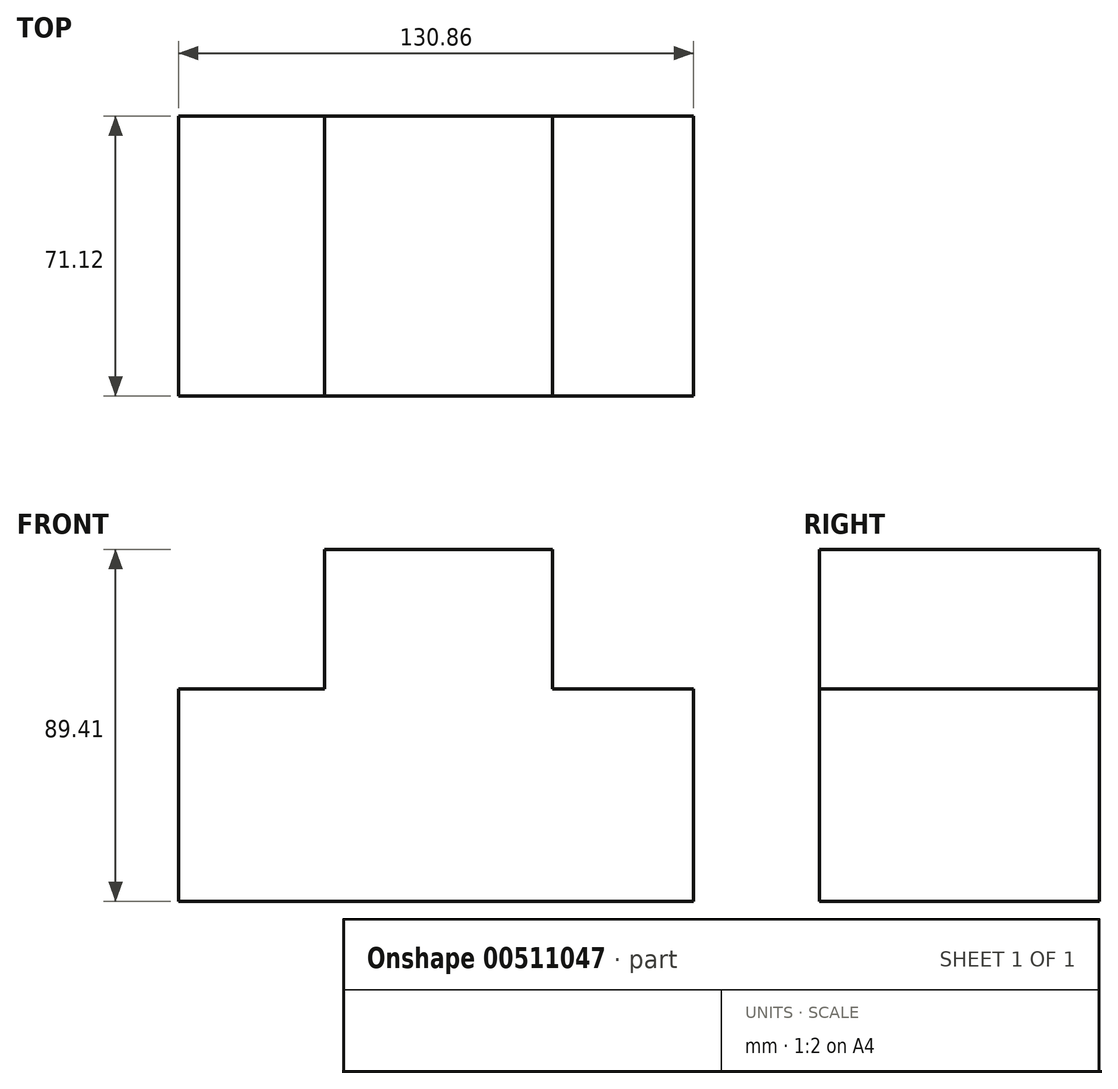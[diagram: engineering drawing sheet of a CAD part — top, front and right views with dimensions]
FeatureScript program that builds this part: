
annotation { "Feature Type Name" : "Feature", "Feature Type Description" : "" }
export const myFeature = defineFeature(function(context is Context, id is Id, definition is map)
    precondition{}
    {
        {
            var Q0;
            Q0=qCreatedBy(makeId("Front.planeOp"),FACE);
            var sketch = newSketch(context, id + "F0", { "sketchPlane" : qUnion([Q0])});
            skLineSegment(sketch, "E0.bottom", {"start": v(-66.27, 59.04) * mm, "end": v(64.59, 59.04) * mm});
            skLineSegment(sketch, "E0.top", {"start": v(-66.27, -48.92) * mm, "end": v(64.59, -48.92) * mm});
            skLineSegment(sketch, "E0.left", {"start": v(-66.27, 59.04) * mm, "end": v(-66.27, -48.92) * mm});
            skLineSegment(sketch, "E0.right", {"start": v(64.59, 59.04) * mm, "end": v(64.59, -48.92) * mm});
            skLineSegment(sketch, "E1", {"start": v(-66.27, 5.06) * mm, "end": v(64.59, 5.06) * mm});
            skLineSegment(sketch, "E2", {"start": v(28.68, 5.06) * mm, "end": v(28.68, 40.49) * mm});
            skLineSegment(sketch, "E3", {"start": v(28.68, 40.49) * mm, "end": v(-29.16, 40.49) * mm});
            skLineSegment(sketch, "E4", {"start": v(-29.16, 40.49) * mm, "end": v(-29.16, 5.06) * mm});
            skSolve(sketch);
        }
        {
            var Q0;
            {var subQ0=sQuery(id+"F0.wireOp",EDGE,"E2");Q0=makeQuery(id+"F0.imprint","IMPRINT",FACE,{"disambiguationData":[TD([[makeQuery(id+"F0.imprint","IMPRINT",EDGE,{"derivedFrom":subQ0}),1.0]])]});}
            var Q1;
            {var subQ1=sQuery(id+"F0.wireOp",EDGE,"E0.top");Q1=makeQuery(id+"F0.imprint","IMPRINT",FACE,{"disambiguationData":[TD([[makeQuery(id+"F0.imprint","IMPRINT",EDGE,{"derivedFrom":subQ1}),1.0]])]});}
            extrude(context, id + "F1", {"entities" : qUnion([Q0, Q1]), "depth" : 71.12 * mm});
        }
    });
